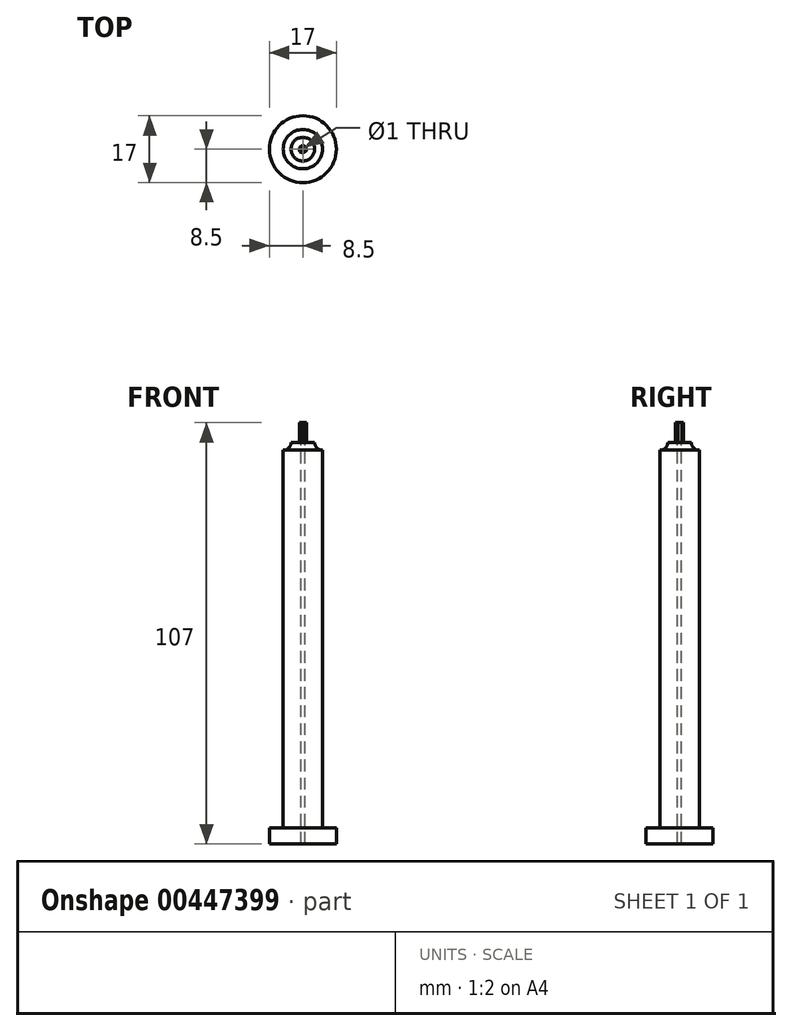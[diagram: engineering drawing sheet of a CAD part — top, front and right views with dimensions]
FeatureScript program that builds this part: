
annotation { "Feature Type Name" : "Feature", "Feature Type Description" : "" }
export const myFeature = defineFeature(function(context is Context, id is Id, definition is map)
    precondition{}
    {
        {
            var Q0;
            Q0=qCreatedBy(makeId("Top.planeOp"),FACE);
            var sketch = newSketch(context, id + "F0", { "sketchPlane" : qUnion([Q0])});
            skCircle(sketch, "E0", {"center": v(0, 0) * mm, "radius": 8.5 * mm});
            skSolve(sketch);
        }
        {
            var Q0;
            Q0=qSketchRegion(id+"F0",true);
            extrude(context, id + "F1", {"entities" : qUnion([Q0]), "depth" : 4 * mm});
        }
        {
            var Q0;
            Q0=qCreatedBy(makeId("Top.planeOp"),FACE);
            var sketch = newSketch(context, id + "F2", { "sketchPlane" : qUnion([Q0])});
            skCircle(sketch, "E1", {"center": v(0, 0) * mm, "radius": 5 * mm});
            skSolve(sketch);
        }
        {
            var Q0;
            Q0=qSketchRegion(id+"F2",true);
            extrude(context, id + "F3", {"entities" : qUnion([Q0]), "operationType" : NewBodyOperationType.ADD, "depth" : 100 * mm});
        }
        {
            var Q0;
            Q0=qCreatedBy(makeId("Right.planeOp"),FACE);
            var sketch = newSketch(context, id + "F4", { "sketchPlane" : qUnion([Q0])});
            skLineSegment(sketch, "E2", {"start": v(0, 102) * mm, "end": v(0, 100) * mm});
            skLineSegment(sketch, "E3", {"start": v(0, 100) * mm, "end": v(5, 100) * mm});
            skLineSegment(sketch, "E4", {"start": v(3, 102) * mm, "end": v(0, 102) * mm});
            skArc(sketch, "E5", {"start": v(3, 102) * mm, "mid": v(3.59, 100.59) * mm, "end": v(5, 100) * mm});
            skSolve(sketch);
        }
        {
            var Q0;
            Q0=makeQuery(id+"F4.imprint","IMPRINT",FACE,{"disambiguationData":[TD([[makeQuery(id+"F4.imprint","IMPRINT",EDGE,{"derivedFrom":sQuery(id+"F4.wireOp",EDGE,"E2")}),1.0]])]});
            var Q1;
            Q1=sQuery(id+"F4.wireOp",EDGE,"E2");
            revolve(context, id + "F5", {"operationType" : NewBodyOperationType.ADD, "entities" : qUnion([Q0]), "axis" : qUnion([Q1]), "revolveType" : RevolveType.FULL});
        }
        {
            var Q0;
            Q0=makeQuery(id+"F5.opRevolve","SWEPT_FACE",FACE,{"disambiguationData":[OSD([sQuery(id+"F4.wireOp",EDGE,"E4")])]});
            var sketch = newSketch(context, id + "F6", { "sketchPlane" : qUnion([Q0])});
            skCircle(sketch, "E6.cCircle", {"center": v(0, 0) * mm, "radius": 0.87 * mm, "construction": true});
            skLineSegment(sketch, "E6.0", {"start": v(0.9, -0.42) * mm, "end": v(0.09, -1) * mm});
            skLineSegment(sketch, "E6.1", {"start": v(0.09, -1) * mm, "end": v(-0.82, -0.57) * mm});
            skLineSegment(sketch, "E6.2", {"start": v(-0.82, -0.57) * mm, "end": v(-0.9, 0.42) * mm});
            skLineSegment(sketch, "E6.3", {"start": v(-0.9, 0.42) * mm, "end": v(-0.09, 1) * mm});
            skLineSegment(sketch, "E6.4", {"start": v(-0.09, 1) * mm, "end": v(0.82, 0.57) * mm});
            skLineSegment(sketch, "E6.5", {"start": v(0.82, 0.57) * mm, "end": v(0.9, -0.42) * mm});
            skPoint(sketch, "E6.0.midPoint", {"position": v(0.5, -0.7) * mm});
            skSolve(sketch);
        }
        {
            var Q0;
            Q0=makeQuery(id+"F6.imprint","IMPRINT",FACE,{"disambiguationData":[TD([[makeQuery(id+"F6.imprint","IMPRINT",EDGE,{"derivedFrom":sQuery(id+"F6.wireOp",EDGE,"E6.0")}),-1.0]])]});
            extrude(context, id + "F7", {"entities" : qUnion([Q0]), "operationType" : NewBodyOperationType.ADD, "depth" : 5 * mm});
        }
        {
            var Q0;
            Q0=makeQuery(id+"F7.opExtrude","CAP_FACE",FACE,{"disambiguationData":[OSD([sQuery(id+"F6.wireOp",EDGE,"E6.0"),sQuery(id+"F6.wireOp",EDGE,"E6.1"),sQuery(id+"F6.wireOp",EDGE,"E6.2"),sQuery(id+"F6.wireOp",EDGE,"E6.3"),sQuery(id+"F6.wireOp",EDGE,"E6.4"),sQuery(id+"F6.wireOp",EDGE,"E6.5")])],"isStart":false});
            var sketch = newSketch(context, id + "F8", { "sketchPlane" : qUnion([Q0])});
            skCircle(sketch, "E7", {"center": v(0, 0) * mm, "radius": 0.5 * mm});
            skSolve(sketch);
        }
        {
            var Q0;
            Q0 = qSketchRegion(id + "F8", true);
            extrude(context, id + "F9", {"entities" : qUnion([Q0]), "operationType" : NewBodyOperationType.REMOVE, "oppositeDirection" : true, "depth" : 110.1 * mm});
        }
    });
